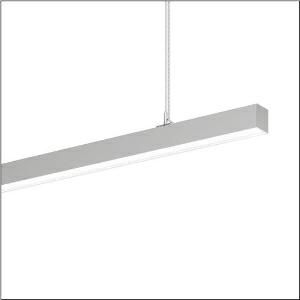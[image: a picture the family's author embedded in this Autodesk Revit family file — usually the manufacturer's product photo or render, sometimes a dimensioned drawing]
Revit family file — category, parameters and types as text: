
# Revit family: silica_r__21_51mx33da47sb_3209
name_source: partatom
category: Lighting Fixtures
units: mm (PartAtom-declared; Revit-internal decimal feet)

## family parameters
Cut with Voids When Loaded = No
Host = Face
Light Source = No
Part Type = Normal
Room Calculation Point = No
Round Connector Dimension = Use Diameter
Shared = No

## types (1)
- --- (1 x LED, 5910 lm, 38.4 W, 4000K)
    Apparent Load = 38 VA
    CIE Flux Codes = 78 96 99 55 100
    Color Rendering = 80
    Color Temperature = 4000K
    Default Elevation = 1800 mm
    Description = Silica® 21, office luminaire, primary optical cover: prismatic diffuser, of PMMA, CAT 2 (L<= 3000cd/m²), light emission: direct/indirect distribution, primary light characteristic: symmetric, installation type: suspended mounting, LED, rated luminous flux: 5.910lm, luminous efficacy: 154lm/W, light colour: 840, colour temperature: 4000K, with terminal, 3+2-pole, max. 2.5mm², mains connection: 220..240V, AC, 50/60Hz, rated input power: 38.4W, luminaire housing, of aluminium, metallic grey (RAL 9006), length: 1.204mm, width: 53mm, height: 53mm, protection rating (complete): IP20, insulation class (complete): insulation class I (protective earthing), certification: CE, permissible operating ambient temperature: 0..+35°C, standard: EN 50419, packaging unit: 1 piece
    Height = 53 mm
    Lamp = 1 x LED
    Lamp Light Flux = 5910 lm
    Lamp Power = 38.4 W
    Lamp count = 1
    Length = 1204 mm
    Luminous efficacy = 154 lm/W
    Manufacturer = Siteco
    ModVariant = No
    Model = 51MX33DA47SB
    Mounting Place = Ceiling
    Mounting Type = Pendant
    Number of Poles = 1
    OnlyDefault = Yes
    Power Factor = 1
    Product Name = Silica® 21
    Product group = office luminaire | ceiling pendant
    ProductGroupID = 902
    Protection Class = Protection class I
    Protection Degree = IP 20
    RLX_Detail_Level = 1
    RLX_Emergency_Light_Flux = 0 lm
    RLX_Emergency_Type = 0
    RLX_Emergency_Type_DB = No
    RlxData = <blob elided: 23137 chars, md5=d72c10eb>
    Socket = socket
    Standby Power = 0 W
    System Light Flux = 5910 lm
    System Power = 38 W
    Type Comments = factory setting: luminous flux: 100 % | dim-lin: 254 | 323 mA
    Type Image = l_1313621.jpg
    URL = http://relux.com
    VarID = @adj_067105
    Voltage = 0 V
    Weight = 0.00 kg
    Width = 53 mm

## geometry (parser evidence)
native form markers: Blend x4, Sweep x12
no freeform markers — native parametric forms only
